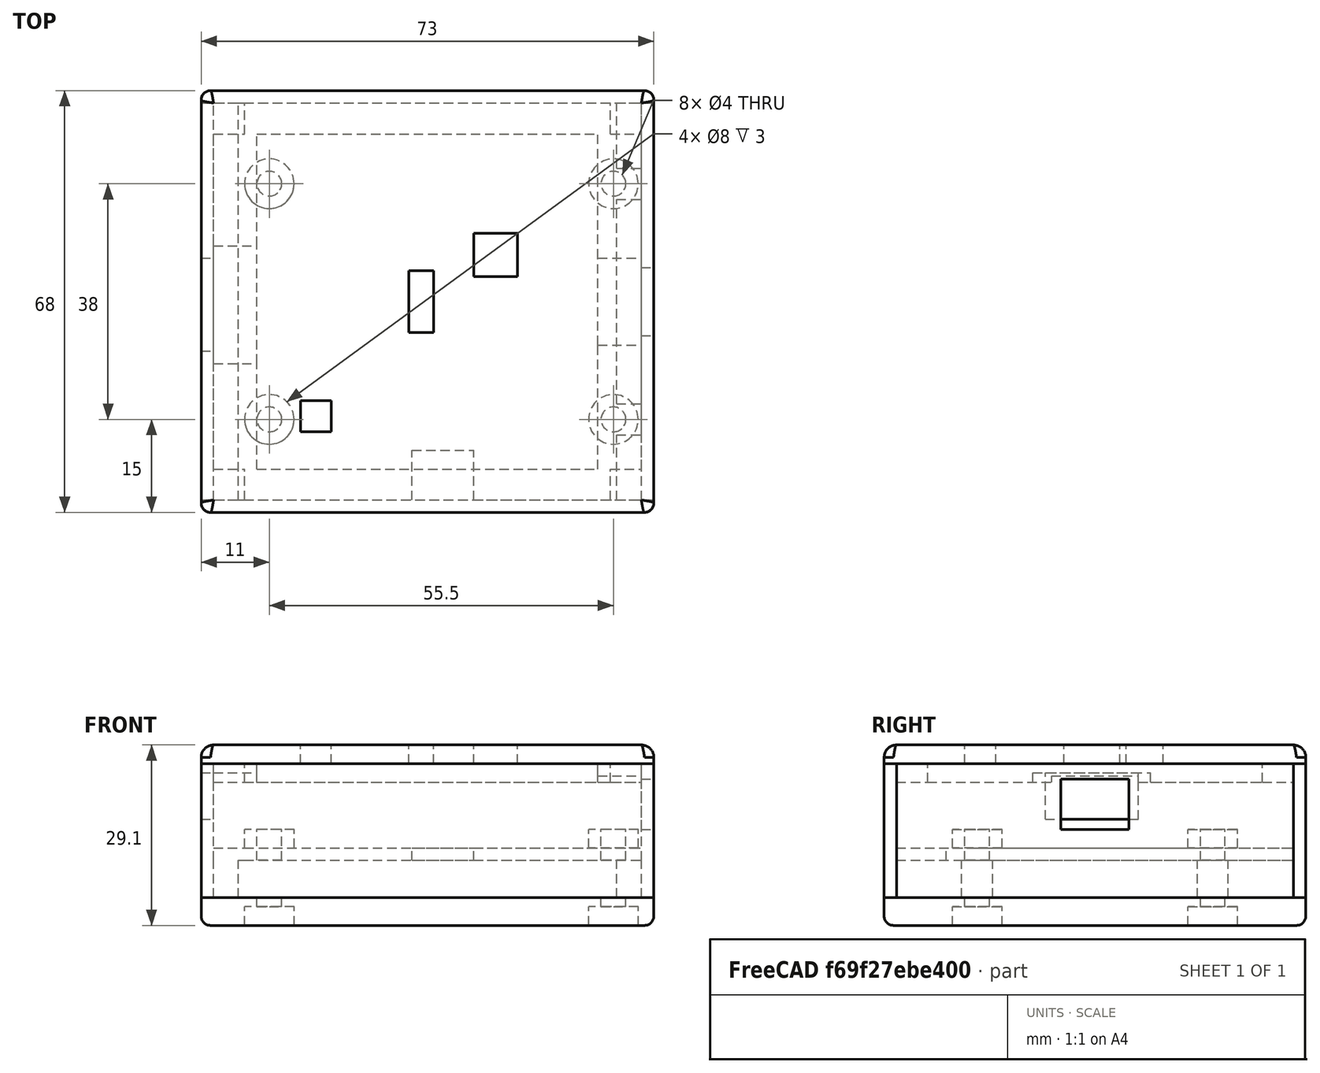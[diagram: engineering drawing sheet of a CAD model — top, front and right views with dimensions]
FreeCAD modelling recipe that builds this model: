
FCSTD DOCUMENT  (FreeCAD 0.14R3700 (Git))
Label: USB_Charger
License: CC-BY 3.0
LicenseURL: http://creativecommons.org/licenses/by/3.0/
objects: Part::Box×32, Part::Cylinder×16, Part::Cut×16, Part::MultiFuse×6, Part::Fillet×6
note: 76 computed .brp shape members not serialized (recipe doc carries the construction recipe); baked Part::Feature solids carry a one-line shape summary decoded from their .brp

FEATURE [Part::Box] Box  label="Cube"
  Height = 2
  Length = 64
  Width = 64
FEATURE [Part::Cylinder] Cylinder003
  Angle = 360
  Height = 5
  Placement = pos=(4,51,0) rot=(0,0,1;0rad)
  Radius = 2
FEATURE [Part::Cylinder] Cylinder004
  Angle = 360
  Height = 3
  Placement = pos=(4,13,2) rot=(0,0,1;0rad)
  Radius = 4
FEATURE [Part::Cylinder] Cylinder005
  Angle = 360
  Height = 3
  Placement = pos=(59.5,13,2) rot=(0,0,1;0rad)
  Radius = 4
FEATURE [Part::Cylinder] Cylinder006
  Angle = 360
  Height = 3
  Placement = pos=(4,51,2) rot=(0,0,1;0rad)
  Radius = 4
FEATURE [Part::Cylinder] Cylinder007
  Angle = 360
  Height = 3
  Placement = pos=(59.5,51,2) rot=(0,0,1;0rad)
  Radius = 4
FEATURE [Part::Cylinder] Cylinder010
  Angle = 360
  Height = 5
  Placement = pos=(59.5,51,0) rot=(0,0,1;0rad)
  Radius = 2
FEATURE [Part::Cylinder] Cylinder011
  Angle = 360
  Height = 5
  Placement = pos=(59.5,13,0) rot=(0,0,1;0rad)
  Radius = 2
FEATURE [Part::Box] Box001  label="Cube001"
  Height = 2
  Length = 5
  Placement = pos=(-5,0,0) rot=(0,0,1;0rad)
  Width = 64
FEATURE [Part::Box] Box002  label="Cube002"
  Height = 2
  Length = 10
  Placement = pos=(27,0,0) rot=(0,0,1;0rad)
  Width = 8
FEATURE [Part::Box] Box003  label="Cube003"
  Height = 21.6
  Length = 73
  Placement = pos=(-7,-2,-6) rot=(0,0,1;0rad)
  Width = 2
FEATURE [Part::Box] Box004  label="Cube004"
  Height = 21.6
  Length = 73
  Placement = pos=(-7,64,-6) rot=(0,0,1;0rad)
  Width = 2
FEATURE [Part::Box] Box006  label="Cube006"
  Height = 15.6
  Length = 2
  Placement = pos=(64,0,0) rot=(0,0,1;0rad)
  Width = 26.5
FEATURE [Part::Box] Box007  label="Cube007"
  Height = 15.6
  Length = 2
  Placement = pos=(64,37.5,0) rot=(0,0,1;0rad)
  Width = 26.5
FEATURE [Part::Box] Box008  label="Cube008"
  Height = 5
  Length = 2
  Placement = pos=(64,26.5,0) rot=(0,0,1;0rad)
  Width = 11
FEATURE [Part::Box] Box009  label="Cube009"
  Height = 2.5
  Length = 2
  Placement = pos=(64,26.5,13.1) rot=(0,0,1;0rad)
  Width = 11
FEATURE [Part::Box] Box010  label="Cube010"
  Height = 14.1
  Length = 2
  Placement = pos=(-7,39,0) rot=(0,0,1;0rad)
  Width = 25
FEATURE [Part::Box] Box011  label="Cube011"
  Height = 14.1
  Length = 2
  Placement = pos=(-7,0,0) rot=(0,0,1;0rad)
  Width = 24
FEATURE [Part::Box] Box012  label="Cube012"
  Height = 6.6
  Length = 2
  Placement = pos=(-7,24,0) rot=(0,0,1;0rad)
  Width = 15
FEATURE [Part::Box] Box013  label="Cube013"
  Height = 1.5
  Length = 2
  Placement = pos=(-7,0,14.1) rot=(0,0,1;0rad)
  Width = 64
FEATURE [Part::Box] Box017  label="Cube017"
  Height = 6
  Length = 2
  Placement = pos=(-7,0,-6) rot=(0,0,1;0rad)
  Width = 64
FEATURE [Part::Box] Box018  label="Cube018"
  Height = 6
  Length = 2
  Placement = pos=(64,0,-6) rot=(0,0,1;0rad)
  Width = 64
FEATURE [Part::Box] Box019  label="Cube019"
  Height = 6
  Length = 4
  Placement = pos=(-5,0,-6) rot=(0,0,1;0rad)
  Width = 64
FEATURE [Part::Box] Box020  label="Cube020"
  Height = 6
  Length = 4
  Placement = pos=(60,0,-6) rot=(0,0,1;0rad)
  Width = 10.5
FEATURE [Part::Box] Box023  label="Cube023"
  Height = 4.5
  Length = 73
  Placement = pos=(-7,-2,-10.5) rot=(0,0,1;0rad)
  Width = 68
FEATURE [Part::Cylinder] Cylinder012
  Angle = 360
  Height = 10
  Placement = pos=(4,13,-10.5) rot=(0,0,1;0rad)
  Radius = 2
FEATURE [Part::Cylinder] Cylinder014
  Angle = 360
  Height = 10
  Placement = pos=(59.5,13,-10.5) rot=(0,0,1;0rad)
  Radius = 2
FEATURE [Part::Cylinder] Cylinder015
  Angle = 360
  Height = 10
  Placement = pos=(4,51,-10.5) rot=(0,0,1;0rad)
  Radius = 2
FEATURE [Part::Cylinder] Cylinder016
  Angle = 360
  Height = 3
  Placement = pos=(4,13,-10.5) rot=(0,0,1;0rad)
  Radius = 4
FEATURE [Part::Cylinder] Cylinder017
  Angle = 360
  Height = 3
  Placement = pos=(59.5,51,-10.5) rot=(0,0,1;0rad)
  Radius = 4
FEATURE [Part::Cylinder] Cylinder018
  Angle = 360
  Height = 3
  Placement = pos=(59.5,13,-10.5) rot=(0,0,1;0rad)
  Radius = 4
FEATURE [Part::Cylinder] Cylinder019
  Angle = 360
  Height = 3
  Placement = pos=(4,51,-10.5) rot=(0,0,1;0rad)
  Radius = 4
FEATURE [Part::Cylinder] Cylinder
  Angle = 360
  Height = 5
  Placement = pos=(4,13,0) rot=(0,0,1;0rad)
  Radius = 2
FEATURE [Part::Cut] Cut
  Base = -> Box
  Tool = -> Box002
FEATURE [Part::MultiFuse] Fusion001
  Shapes = -> [Box001,Cut]
FEATURE [Part::MultiFuse] Fusion002
  Shapes = -> [Fusion001,Cylinder004,Cylinder005,Cylinder006,Cylinder007]
FEATURE [Part::Cut] Cut001
  Base = -> Fusion002
  Tool = -> Cylinder010
FEATURE [Part::Cut] Cut002
  Base = -> Cut001
  Tool = -> Cylinder003
FEATURE [Part::Cut] Cut003
  Base = -> Cut002
  Tool = -> Cylinder
FEATURE [Part::Cut] Cut004
  Base = -> Cut003
  Tool = -> Cylinder011
FEATURE [Part::Box] Box032  label="Cube032"
  Height = 6
  Length = 4
  Placement = pos=(60,53.5,-6) rot=(0,0,1;0rad)
  Width = 10.5
FEATURE [Part::Box] Box033  label="Cube033"
  Height = 6
  Length = 4
  Placement = pos=(60,15.5,-6) rot=(0,0,1;0rad)
  Width = 33
FEATURE [Part::Fillet] Fillet
  Base = -> Box004
  Edges = 2 edges r=1.5: [Edge3,Edge7]
FEATURE [Part::Fillet] Fillet003
  Base = -> Box003
  Edges = 2 edges r=1.5: [Edge1,Edge5]
FEATURE [Part::MultiFuse] Fusion007
  Shapes = -> [Box006,Box007,Box008,Box009,Box018]
FEATURE [Part::MultiFuse] Fusion
  Shapes = -> [Box013,Box011,Box017,Box012,Box010]
FEATURE [Part::MultiFuse] Fusion008
  Shapes = -> [Cut004,Box019,Box020,Box032,Box033]
FEATURE [Part::Box] Box034  label="Cube034"
  Height = 3
  Length = 73
  Placement = pos=(-7,-2,15.6) rot=(0,0,1;0rad)
  Width = 68
FEATURE [Part::Box] Box035  label="Cube035"
  Height = 4
  Length = 4
  Placement = pos=(26.5,27,15) rot=(0,0,1;0rad)
  Width = 10
FEATURE [Part::Cylinder] Cylinder013
  Angle = 360
  Height = 10
  Placement = pos=(59.5,51,-10.5) rot=(0,0,1;0rad)
  Radius = 2
FEATURE [Part::Cut] Cut014
  Base = -> Box023
  Tool = -> Cylinder019
FEATURE [Part::Cut] Cut015
  Base = -> Cut014
  Tool = -> Cylinder018
FEATURE [Part::Cut] Cut016
  Base = -> Cut015
  Tool = -> Cylinder017
FEATURE [Part::Cut] Cut017
  Base = -> Cut016
  Tool = -> Cylinder016
FEATURE [Part::Cut] Cut018
  Base = -> Cut017
  Tool = -> Cylinder012
FEATURE [Part::Cut] Cut019
  Base = -> Cut018
  Tool = -> Cylinder015
FEATURE [Part::Cut] Cut020
  Base = -> Cut019
  Tool = -> Cylinder014
FEATURE [Part::Cut] Cut021
  Base = -> Cut020
  Tool = -> Cylinder013
FEATURE [Part::Fillet] Fillet006
  Base = -> Cut021
  Edges = 4 edges r=1.5: [Edge1,Edge3,Edge6,Edge19]
FEATURE [Part::Fillet] Fillet007
  Base = -> Fillet006
  Edges = 8 edges r=1.5: [Edge4,Edge20,Edge22,Edge24,Edge25,Edge26,Edge27,Edge28]
FEATURE [Part::Box] Box036  label="Cube036"
  Height = 4
  Length = 5
  Placement = pos=(9,11,15) rot=(0,0,1;0rad)
  Width = 5
FEATURE [Part::Box] Box037  label="Cube037"
  Height = 4
  Length = 7
  Placement = pos=(37,36,15) rot=(0,0,1;0rad)
  Width = 7
FEATURE [Part::Box] Box038  label="Cube038"
  Height = 3
  Length = 7
  Placement = pos=(-5,5,12.6) rot=(0,0,1;0rad)
  Width = 17
FEATURE [Part::Box] Box040  label="Cube040"
  Height = 3
  Length = 7
  Placement = pos=(57,5,12.6) rot=(0,0,1;0rad)
  Width = 20
FEATURE [Part::Box] Box042  label="Cube042"
  Height = 3
  Length = 59
  Placement = pos=(0,59,12.6) rot=(0,0,1;0rad)
  Width = 5
FEATURE [Part::Box] Box043  label="Cube043"
  Height = 3
  Length = 59
  Placement = pos=(0,0,12.6) rot=(0,0,1;0rad)
  Width = 5
FEATURE [Part::Fillet] Fillet008
  Base = -> Box034
  Edges = 4 edges r=1.5: [Edge1,Edge3,Edge5,Edge7]
FEATURE [Part::Fillet] Fillet009
  Base = -> Fillet008
  Edges = 8 edges r=2: [Edge1,Edge5,Edge6,Edge7,Edge8,Edge9,Edge10,Edge11]
FEATURE [Part::Cut] Cut022
  Base = -> Fillet009
  Tool = -> Box035
FEATURE [Part::Cut] Cut023
  Base = -> Cut022
  Tool = -> Box037
FEATURE [Part::Cut] Cut024
  Base = -> Cut023
  Tool = -> Box036
FEATURE [Part::Box] Box044  label="Cube044"
  Height = 2
  Length = 7
  Placement = pos=(57,25,13.6) rot=(0,0,1;0rad)
  Width = 14
FEATURE [Part::Box] Box045  label="Cube045"
  Height = 3
  Length = 7
  Placement = pos=(57,39,12.6) rot=(0,0,1;0rad)
  Width = 20
FEATURE [Part::Box] Box046  label="Cube046"
  Height = 1.5
  Length = 7
  Placement = pos=(-5,22,14.1) rot=(0,0,1;0rad)
  Width = 19
FEATURE [Part::Box] Box047  label="Cube047"
  Height = 3
  Length = 7
  Placement = pos=(-5,41,12.6) rot=(0,0,1;0rad)
  Width = 18
FEATURE [Part::MultiFuse] Fusion009
  Shapes = -> [Box038,Box043,Box046,Box047,Box042,Box040,Box044,Box045]
